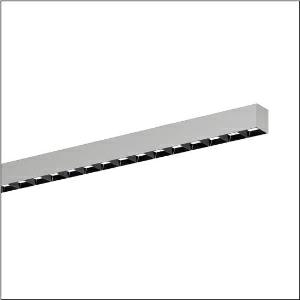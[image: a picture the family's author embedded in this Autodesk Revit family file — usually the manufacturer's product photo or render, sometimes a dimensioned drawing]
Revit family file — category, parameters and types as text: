
# Revit family: silica_r__21_51mx22dc3asb_7d31
name_source: partatom
category: Lighting Fixtures
units: mm (PartAtom-declared; Revit-internal decimal feet)

## family parameters
Cut with Voids When Loaded = No
Host = Face
Light Source = No
Part Type = Normal
Room Calculation Point = No
Round Connector Dimension = Use Diameter
Shared = No

## types (1)
- --- (1 x LED, 10800 lm, 69.2 W, 3000K)
    Apparent Load = 69 VA
    CIE Flux Codes = 86 100 100 100 100
    Color Rendering = 80
    Color Temperature = 3000K
    Default Elevation = 1800 mm
    Description = Silica® 21, office luminaire, primary light control with darklight reflector, of PMMA, black, CAT 2 (L<= 3000cd/m²), light emission: direct distribution, primary light characteristic: symmetric, installation type: surface-mounted, LED, rated luminous flux: 10.800lm, luminous efficacy: 156lm/W, light colour: 830, colour temperature: 3000K, with terminal, 3+2-pole, max. 2.5mm², mains connection: 220..240V, AC, 50/60Hz, rated input power: 69.2W, luminaire housing, of aluminium, metallic grey (RAL 9006), length: 3.004mm, width: 53mm, height: 53mm, protection rating (complete): IP20, insulation class (complete): insulation class I (protective earthing), certification: CE, permissible operating ambient temperature: 0..+35°C, standard: EN 50419, packaging unit: 1 piece
    Height = 0 mm  [stored 0 ft]
    Lamp = 1 x LED
    Lamp Light Flux = 10800 lm
    Lamp Power = 69.2 W
    Lamp count = 1
    Length = 3004 mm
    Luminous efficacy = 156 lm/W
    Manufacturer = Siteco
    ModVariant = No
    Model = 51MX22DC3ASB
    Mounting Place = Ceiling
    Mounting Type = Recessed
    Number of Poles = 1
    OnlyDefault = Yes
    Power Factor = 1
    Product Name = Silica® 21
    Product group = office luminaire | ceiling recessed
    ProductGroupID = 401
    Protection Class = Protection class I
    Protection Degree = IP 20
    RLX_Detail_Level = 1
    RLX_Emergency_Light_Flux = 0 lm
    RLX_Emergency_Type = 0
    RLX_Emergency_Type_DB = No
    RlxData = <blob elided: 62785 chars, md5=534692f3>
    Socket = socket
    Standby Power = 0 W
    System Light Flux = 10800 lm
    System Power = 69 W
    Type Comments = factory setting: luminous flux: 100 % | dim-lin: 254 | 392 mA
    Type Image = l_1313585.jpg
    URL = http://relux.com
    VarID = @adj_073945
    Voltage = 0 V
    Weight = 0.00 kg
    Width = 53 mm

note: [stored X ft] marks values corroborated as IEEE doubles in the binary element streams (Revit-internal decimal feet)

## geometry (parser evidence)
native form markers: Blend x4, Sweep x9
no freeform markers — native parametric forms only
